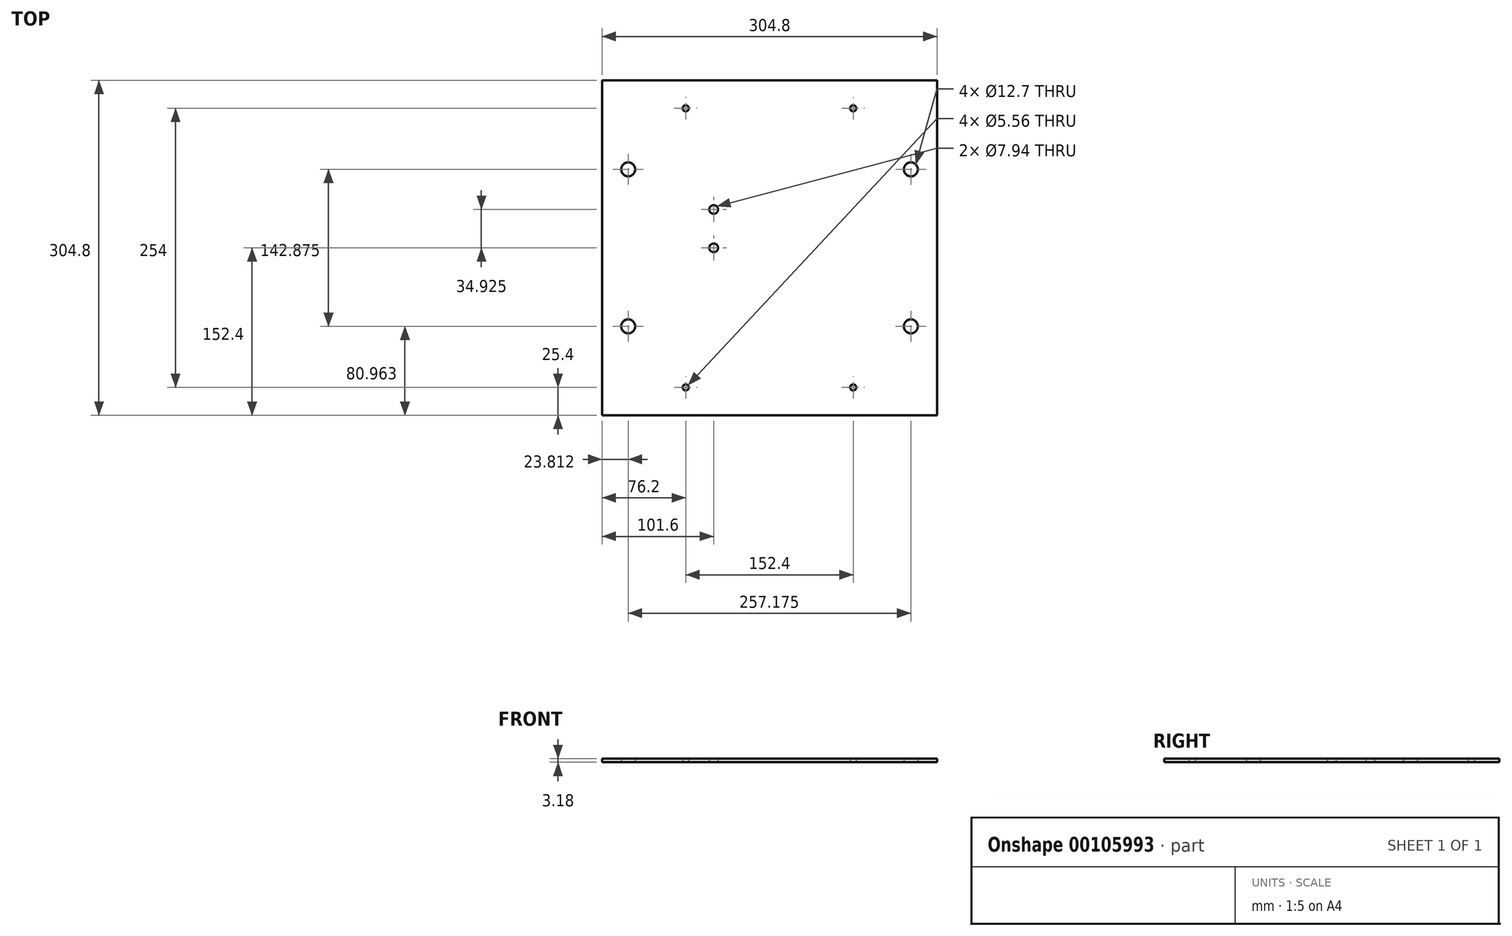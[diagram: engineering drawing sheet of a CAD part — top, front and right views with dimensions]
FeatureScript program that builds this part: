
annotation { "Feature Type Name" : "Feature", "Feature Type Description" : "" }
export const myFeature = defineFeature(function(context is Context, id is Id, definition is map)
    precondition{}
    {
        {
            var Q0;
            Q0=qCreatedBy(makeId("Top.planeOp"),FACE);
            var sketch = newSketch(context, id + "F0", { "sketchPlane" : qUnion([Q0])});
            skLineSegment(sketch, "E0.bottom", {"start": v(-152.4, 152.4) * mm, "end": v(152.4, 152.4) * mm});
            skLineSegment(sketch, "E0.top", {"start": v(-152.4, -152.4) * mm, "end": v(152.4, -152.4) * mm});
            skLineSegment(sketch, "E0.left", {"start": v(-152.4, 152.4) * mm, "end": v(-152.4, -152.4) * mm});
            skLineSegment(sketch, "E0.right", {"start": v(152.4, 152.4) * mm, "end": v(152.4, -152.4) * mm});
            skCircle(sketch, "E1", {"center": v(-128.59, -71.44) * mm, "radius": 6.35 * mm});
            skCircle(sketch, "E2", {"center": v(-76.2, -127) * mm, "radius": 2.78 * mm});
            skLineSegment(sketch, "E3", {"start": v(-152.4, 0) * mm, "end": v(152.4, 0) * mm, "construction": true});
            skLineSegment(sketch, "E4", {"start": v(0, -152.4) * mm, "end": v(0, 152.4) * mm, "construction": true});
            skCircle(sketch, "E5.MirrorC", {"center": v(-128.59, 71.44) * mm, "radius": 6.35 * mm});
            skCircle(sketch, "E6.MirrorC", {"center": v(-76.2, 127) * mm, "radius": 2.78 * mm});
            skLineSegment(sketch, "E7.MirrorCS", {"start": v(0, 152.4) * mm, "end": v(0, -152.4) * mm, "construction": true});
            skCircle(sketch, "E8.MirrorC", {"center": v(128.59, 71.44) * mm, "radius": 6.35 * mm});
            skCircle(sketch, "E9.MirrorC", {"center": v(76.2, 127) * mm, "radius": 2.78 * mm});
            skCircle(sketch, "E10.MirrorC", {"center": v(76.2, -127) * mm, "radius": 2.78 * mm});
            skCircle(sketch, "E11.MirrorC", {"center": v(128.59, -71.44) * mm, "radius": 6.35 * mm});
            skLineSegment(sketch, "E12", {"start": v(-50.8, -152.4) * mm, "end": v(-50.8, 0) * mm, "construction": true});
            skLineSegment(sketch, "E13", {"start": v(-50.8, 0) * mm, "end": v(-50.8, 34.93) * mm, "construction": true});
            skCircle(sketch, "E14", {"center": v(-50.8, 0) * mm, "radius": 3.97 * mm});
            skCircle(sketch, "E15", {"center": v(-50.8, 34.93) * mm, "radius": 3.97 * mm});
            skSolve(sketch);
        }
        {
            var Q0;
            Q0=makeQuery(id+"F0.imprint","IMPRINT",FACE,{"disambiguationData":[TD([[makeQuery(id+"F0.imprint","IMPRINT",EDGE,{"derivedFrom":sQuery(id+"F0.wireOp",EDGE,"E0.bottom")}),-1.0]])]});
            extrude(context, id + "F1", {"entities" : qUnion([Q0]), "depth" : 3.17 * mm});
        }
    });
